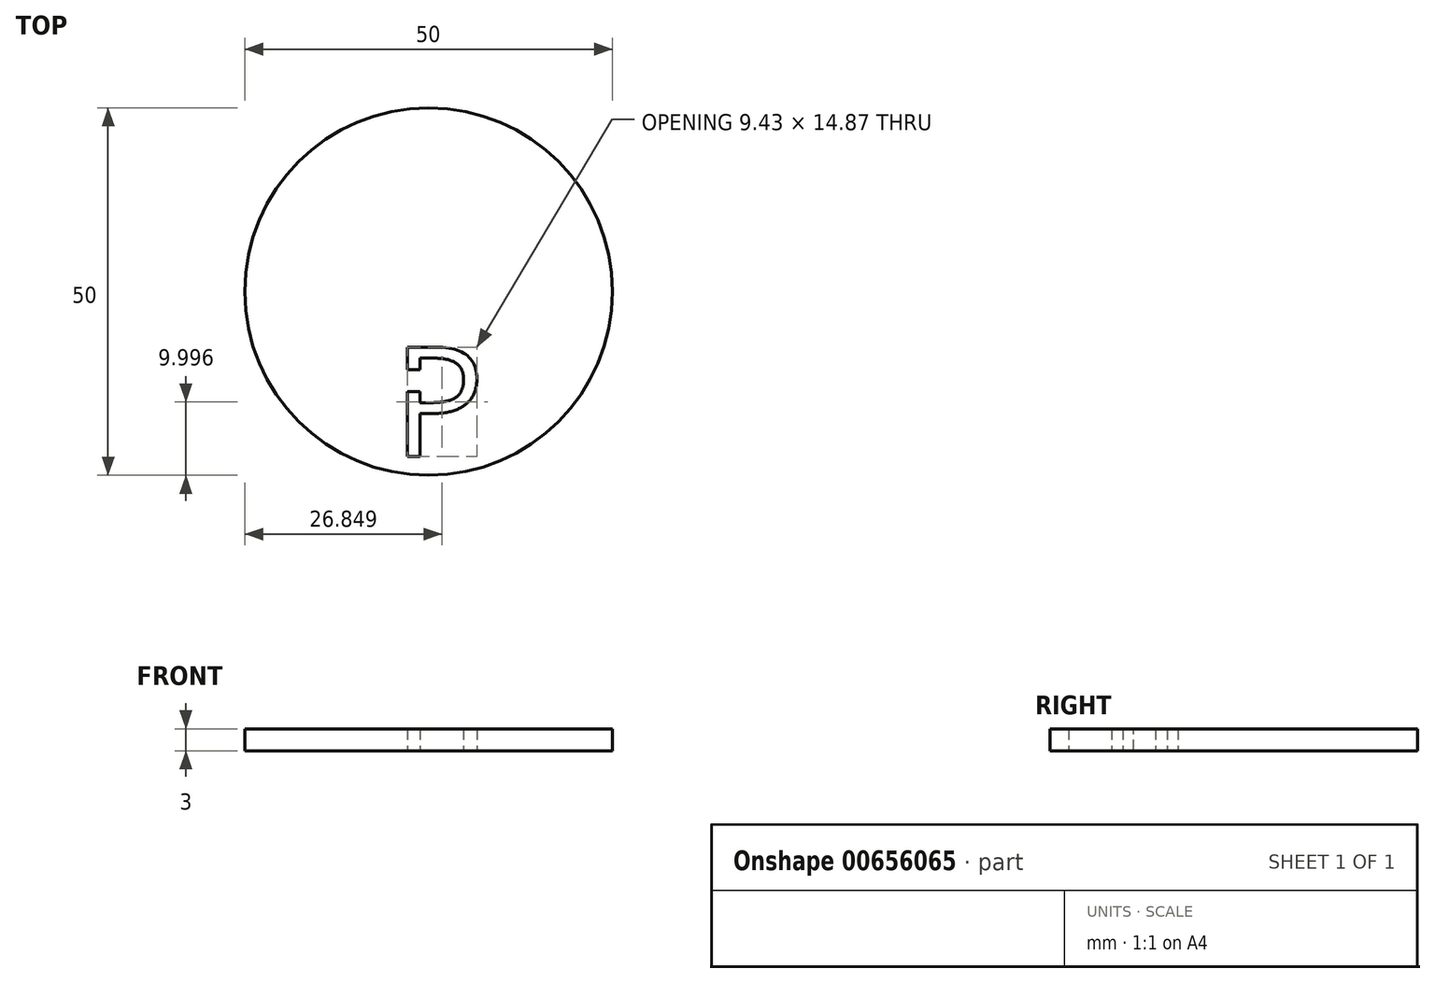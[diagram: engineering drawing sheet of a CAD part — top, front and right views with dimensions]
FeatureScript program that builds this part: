
annotation { "Feature Type Name" : "Feature", "Feature Type Description" : "" }
export const myFeature = defineFeature(function(context is Context, id is Id, definition is map)
    precondition{}
    {
        {
            var Q0;
            Q0=qCreatedBy(makeId("Top.planeOp"),FACE);
            var sketch = newSketch(context, id + "F0", { "sketchPlane" : qUnion([Q0])});
            skCircle(sketch, "E0", {"center": v(0, 0) * mm, "radius": 25 * mm});
            skCircle(sketch, "E1", {"center": v(0, 0) * mm, "radius": 6 * mm, "construction": true});
            skLineSegment(sketch, "E2", {"start": v(0, 0) * mm, "end": v(0, -25) * mm, "construction": true});
            skText(sketch, "E3", { "text": "P", "fontName": "OpenSans-Regular.ttf"});
            const initialGuessF0  = {"E3": [-0.00491, -0.02244, 1, 0, 0.015]};
            skSetInitialGuess(sketch, initialGuessF0);
            skSolve(sketch);
        }
        {
            var Q0;
            Q0=makeQuery(id+"F0.imprint","IMPRINT",FACE,{"disambiguationData":[TD([[makeQuery(id+"F0.imprint","IMPRINT",EDGE,{"derivedFrom":sQuery(id+"F0.wireOp",EDGE,"E0")}),1.0]])]});
            var Q1;
            Q1=makeQuery(id+"F0.imprint","IMPRINT",FACE,{"disambiguationData":[TD([[makeQuery(id+"F0.imprint","IMPRINT",EDGE,{"derivedFrom":sQuery(id+"F0.wireOp",EDGE,"E3.sketch_text.stroke-8")}),1.0]])]});
            extrude(context, id + "F1", {"entities" : qUnion([Q0, Q1]), "depth" : 3 * mm, "offsetDistance" : 25 * mm});
        }
        {
            var Q0;
            Q0=qCreatedBy(makeId("Top.planeOp"),FACE);
            var sketch = newSketch(context, id + "F2", { "sketchPlane" : qUnion([Q0])});
            skLineSegment(sketch, "E4", {"start": v(-9.75, -10.62) * mm, "end": v(0, -10.62) * mm});
            skLineSegment(sketch, "E5", {"start": v(0, -10.62) * mm, "end": v(0, -13.62) * mm});
            skLineSegment(sketch, "E6", {"start": v(0, -13.62) * mm, "end": v(-9.67, -13.62) * mm});
            skLineSegment(sketch, "E7", {"start": v(-9.67, -13.62) * mm, "end": v(-9.75, -10.62) * mm});
            skSolve(sketch);
        }
        {
            var Q0;
            Q0 = qSketchRegion(id + "F2", true);
            extrude(context, id + "F3", {"entities" : qUnion([Q0]), "operationType" : NewBodyOperationType.ADD, "depth" : 3 * mm, "offsetDistance" : 25 * mm});
        }
    });
